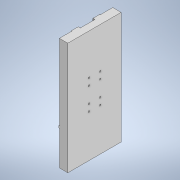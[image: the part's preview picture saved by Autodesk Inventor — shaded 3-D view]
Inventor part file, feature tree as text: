
AUTODESK INVENTOR PART (.ipt)
format: ipt  version: 2020.1 (Build 241239000, 239)  size: 158,208 bytes
history: native  units: mm
features: extrude x4, sketch x4, projected_geometry x3, other x1
ambient origin geometry x8: Origin, YZ Plane, XZ Plane, XY Plane, X Axis, Y Axis, Z Axis, Center Point
bodies: Body1 (feature_tree)
feature tree (12):
  other  "Твердое тело1"
  extrude  "Выдавливание1"  Depth=190.0mm
  extrude  "Выдавливание2"  Depth=30.0mm
  extrude  "Выдавливание3"  Depth=32.0mm
  extrude  "Выдавливание4"  Depth=44.0mm
  sketch  "Эскиз1"
  sketch  "Эскиз2"
  projected_geometry  "Спроецированная петля1"
  sketch  "Эскиз3"
  projected_geometry  "Спроецированная петля2"
  projected_geometry  "Спроецированная петля3"
  sketch  "Эскиз4"
